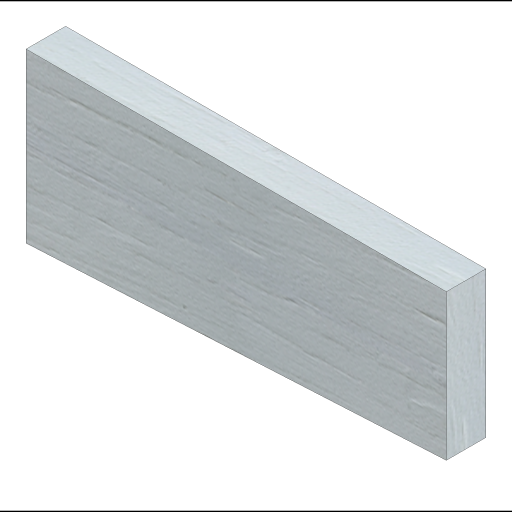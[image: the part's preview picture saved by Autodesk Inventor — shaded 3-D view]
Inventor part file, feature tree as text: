
AUTODESK INVENTOR PART (.ipt)
format: ipt  version: 2023 (Build 270158000, 158)  size: 265,728 bytes
history: native  units: in
note: dims shown in document units (in); Inventor stores cm internally (conversion verified against a paired STEP export)
features: extrude x1, sketch x1
ambient origin geometry x8: Origin, YZ Plane, XZ Plane, XY Plane, X Axis, Y Axis, Z Axis, Center Point
bodies: Body1 (feature_tree)
feature tree (2):
  extrude  "Extrusion2"  Depth=2.0in
  sketch  "Sketch1"  dims[d0=0.0206in d4=2.0in d5=5.0in d6=0.47in d7=0.0in]
